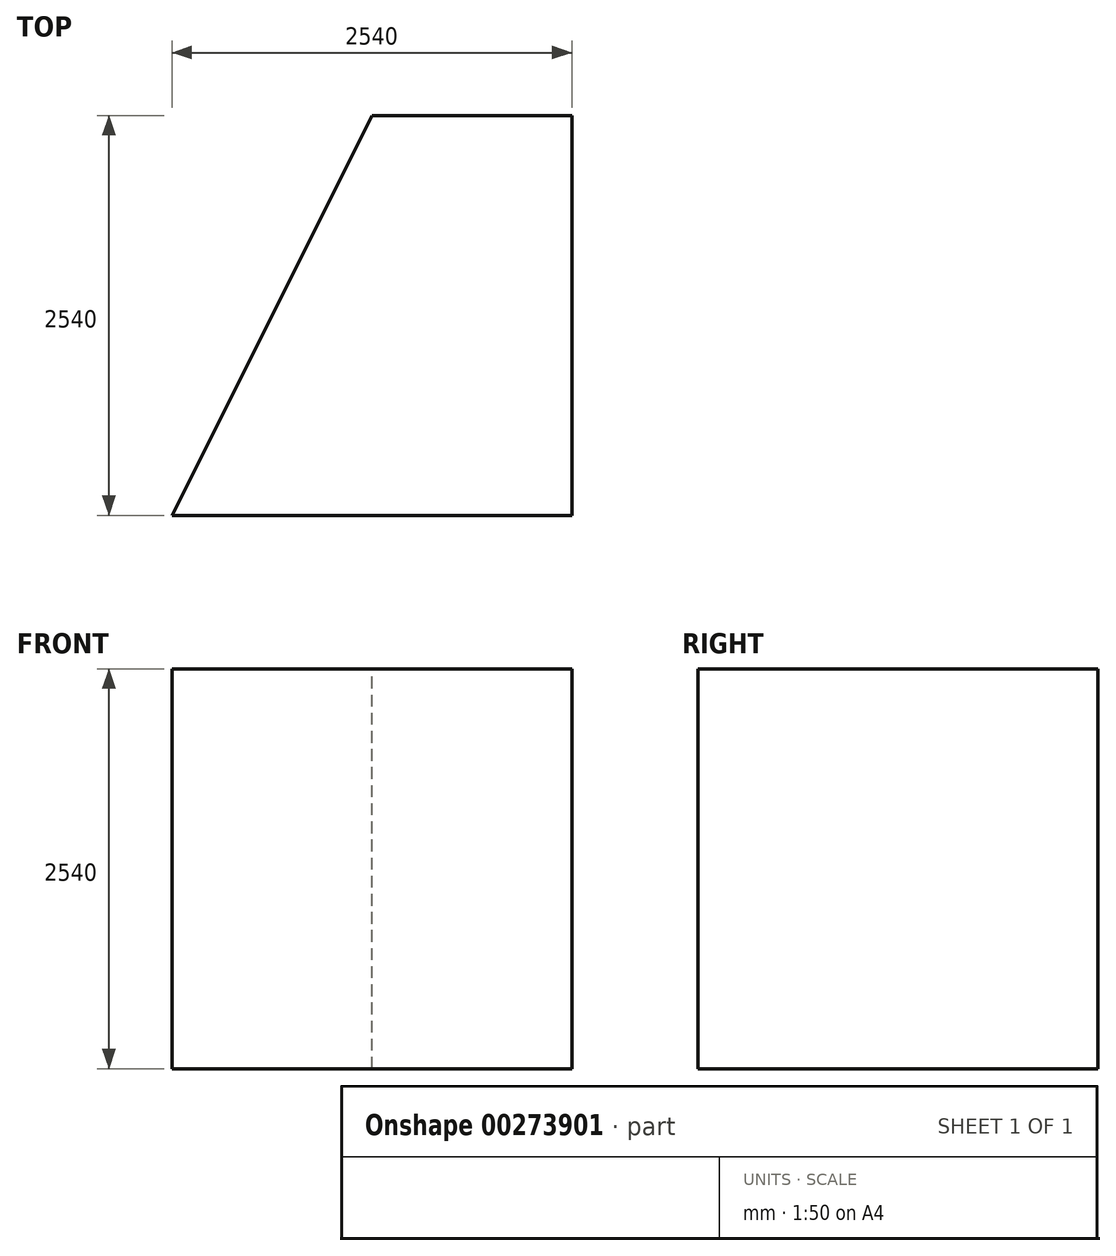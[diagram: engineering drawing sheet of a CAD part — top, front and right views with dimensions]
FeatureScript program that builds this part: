
annotation { "Feature Type Name" : "Feature", "Feature Type Description" : "" }
export const myFeature = defineFeature(function(context is Context, id is Id, definition is map)
    precondition{}
    {
        {
            var Q0;
            Q0=qCreatedBy(makeId("Front.planeOp"),FACE);
            var sketch = newSketch(context, id + "F0", { "sketchPlane" : qUnion([Q0])});
            skLineSegment(sketch, "E0.bottom", {"start": v(-1273.34, 1740.87) * mm, "end": v(1266.66, 1740.87) * mm});
            skLineSegment(sketch, "E0.top", {"start": v(-1273.34, -799.13) * mm, "end": v(1266.66, -799.13) * mm});
            skLineSegment(sketch, "E0.left", {"start": v(-1273.34, 1740.87) * mm, "end": v(-1273.34, -799.13) * mm});
            skLineSegment(sketch, "E0.right", {"start": v(1266.66, 1740.87) * mm, "end": v(1266.66, -799.13) * mm});
            skSolve(sketch);
        }
        {
            var Q0;
            Q0 = qSketchRegion(id + "F0", true);
            extrude(context, id + "F1", {"entities" : qUnion([Q0]), "depth" : 2540 * mm});
        }
        {
            var Q0;
            Q0=makeQuery(id+"F1.opExtrude","SWEPT_FACE",FACE,{"disambiguationData":[OSD([sQuery(id+"F0.wireOp",EDGE,"E0.left")])]});
            cPlane(context, id + "F2", {"entities" : qUnion([Q0]), "cplaneType" : CPlaneType.OFFSET, "offset" : 1270 * mm, "oppositeDirection" : true, "width" : 152.4 * mm, "height" : 152.4 * mm});
        }
        {
            var Q0;
            Q0=qCreatedBy(id+"F2.planeOp",FACE);
            var sketch = newSketch(context, id + "F3", { "sketchPlane" : qUnion([Q0])});
            skLineSegment(sketch, "E1", {"start": v(0, -798.87) * mm, "end": v(0, 1748.19) * mm});
            skSolve(sketch);
        }
        {
            var Q0;
            Q0=sQuery(id+"F3.wireOp",VERTEX,"E1.end");
            var Q1;
            Q1=makeQuery(id+"F1.opExtrude","CAP_VERTEX",VERTEX,{"disambiguationData":[OSD([sQuery(id+"F0.wireOp",EDGE,"E0.top"),sQuery(id+"F0.wireOp",EDGE,"E0.left")])],"isStart":false});
            var Q2;
            Q2=makeQuery(id+"F1.opExtrude","CAP_VERTEX",VERTEX,{"disambiguationData":[OSD([sQuery(id+"F0.wireOp",EDGE,"E0.bottom"),sQuery(id+"F0.wireOp",EDGE,"E0.left")])],"isStart":false});
            cPlane(context, id + "F4", {"entities" : qUnion([Q0, Q1, Q2]), "cplaneType" : CPlaneType.THREE_POINT, "offset" : 25.4 * mm, "width" : 152.4 * mm, "height" : 152.4 * mm});
        }
        {
            var Q0;
            Q0=qCreatedBy(id+"F4.planeOp",FACE);
            var sketch = newSketch(context, id + "F5", { "sketchPlane" : qUnion([Q0])});
            skLineSegment(sketch, "E2", {"start": v(0, 1789.14) * mm, "end": v(0, -799.39) * mm});
            skLineSegment(sketch, "E3", {"start": v(0, -799.39) * mm, "end": v(-2858.92, -799.39) * mm});
            skLineSegment(sketch, "E4", {"start": v(-2858.92, -799.39) * mm, "end": v(-2858.92, 1771.33) * mm});
            skLineSegment(sketch, "E5", {"start": v(-2858.92, 1771.33) * mm, "end": v(0, 1789.14) * mm});
            skSolve(sketch);
        }
        {
            var Q0;
            Q0 = qSketchRegion(id + "F5", true);
            extrude(context, id + "F6", {"entities" : qUnion([Q0]), "operationType" : NewBodyOperationType.REMOVE, "oppositeDirection" : true, "depth" : 2540 * mm});
        }
    });
